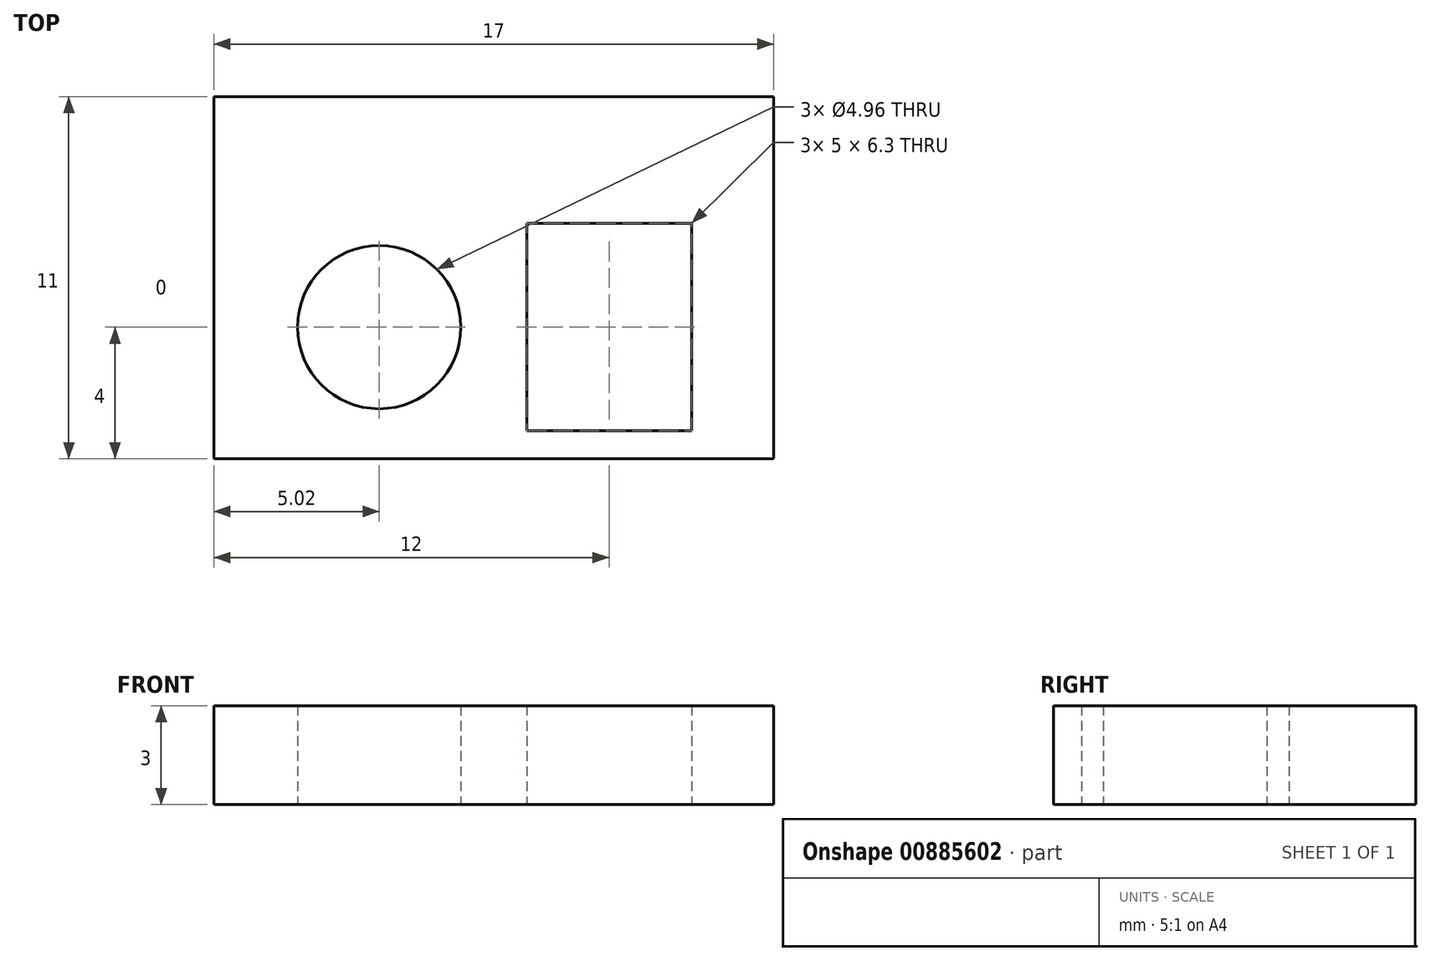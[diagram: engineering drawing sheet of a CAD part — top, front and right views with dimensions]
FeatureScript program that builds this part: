
annotation { "Feature Type Name" : "Feature", "Feature Type Description" : "" }
export const myFeature = defineFeature(function(context is Context, id is Id, definition is map)
    precondition{}
    {
        {
            var Q0;
            Q0=qCreatedBy(makeId("Top.planeOp"),FACE);
            var sketch = newSketch(context, id + "F0", { "sketchPlane" : qUnion([Q0])});
            skLineSegment(sketch, "E0.bottom", {"start": v(0, 0) * mm, "end": v(17, 0) * mm});
            skLineSegment(sketch, "E0.top", {"start": v(0, 11) * mm, "end": v(17, 11) * mm});
            skLineSegment(sketch, "E0.left", {"start": v(0, 0) * mm, "end": v(0, 11) * mm});
            skLineSegment(sketch, "E0.right", {"start": v(17, 0) * mm, "end": v(17, 11) * mm});
            skCircle(sketch, "E1", {"center": v(5.02, 4) * mm, "radius": 2.48 * mm});
            skLineSegment(sketch, "E2.bottom", {"start": v(9.5, 7.15) * mm, "end": v(14.5, 7.15) * mm});
            skLineSegment(sketch, "E2.top", {"start": v(9.5, 0.85) * mm, "end": v(14.5, 0.85) * mm});
            skLineSegment(sketch, "E2.left", {"start": v(9.5, 7.15) * mm, "end": v(9.5, 0.85) * mm});
            skLineSegment(sketch, "E2.right", {"start": v(14.5, 7.15) * mm, "end": v(14.5, 0.85) * mm});
            skSolve(sketch);
        }
        {
            var Q0;
            Q0=makeQuery(id+"F0.imprint","IMPRINT",FACE,{"disambiguationData":[TD([[makeQuery(id+"F0.imprint","IMPRINT",EDGE,{"derivedFrom":sQuery(id+"F0.wireOp",EDGE,"E0.bottom")}),1.0]])]});
            extrude(context, id + "F1", {"entities" : qUnion([Q0]), "depth" : 3 * mm, "offsetDistance" : 25 * mm});
        }
    });
